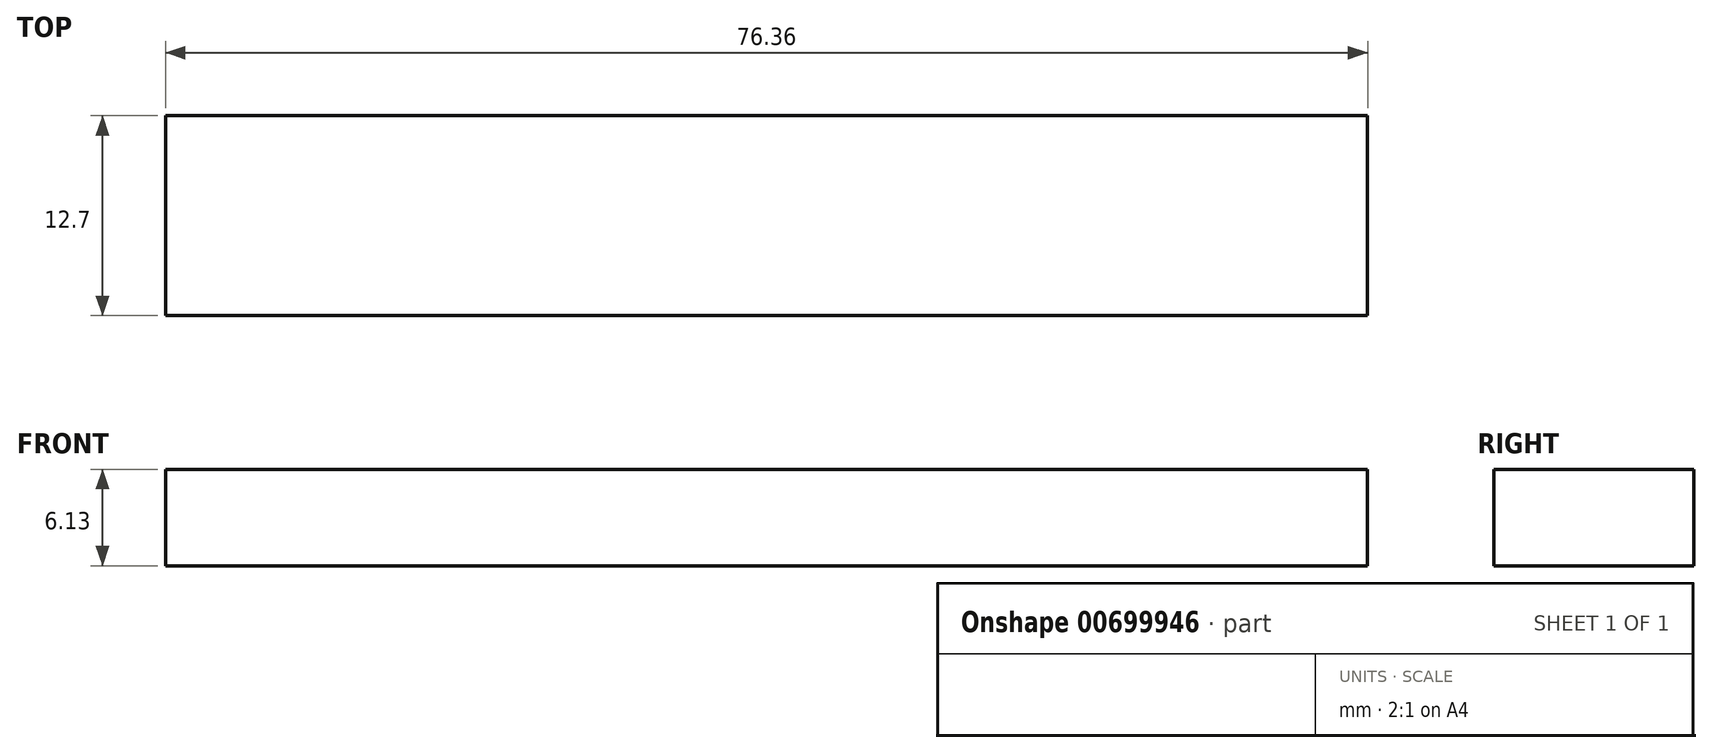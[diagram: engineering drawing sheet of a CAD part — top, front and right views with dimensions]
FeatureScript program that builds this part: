
annotation { "Feature Type Name" : "Feature", "Feature Type Description" : "" }
export const myFeature = defineFeature(function(context is Context, id is Id, definition is map)
    precondition{}
    {
        {
            var Q0;
            Q0=qCreatedBy(makeId("Front.planeOp"),FACE);
            var sketch = newSketch(context, id + "F0", { "sketchPlane" : qUnion([Q0])});
            skLineSegment(sketch, "E0.bottom", {"start": v(-59.82, 26.83) * mm, "end": v(16.54, 26.83) * mm});
            skLineSegment(sketch, "E0.top", {"start": v(-59.82, 20.7) * mm, "end": v(16.54, 20.7) * mm});
            skLineSegment(sketch, "E0.left", {"start": v(-59.82, 26.83) * mm, "end": v(-59.82, 20.7) * mm});
            skLineSegment(sketch, "E0.right", {"start": v(16.54, 26.83) * mm, "end": v(16.54, 20.7) * mm});
            skSolve(sketch);
        }
        {
            var Q0;
            Q0=makeQuery(id+"F0.imprint","IMPRINT",FACE,{"disambiguationData":[TD([[makeQuery(id+"F0.imprint","IMPRINT",EDGE,{"derivedFrom":sQuery(id+"F0.wireOp",EDGE,"E0.bottom")}),-1.0]])]});
            extrude(context, id + "F1", {"entities" : qUnion([Q0]), "depth" : 12.7 * mm, "offsetDistance" : 25.4 * mm});
        }
    });
